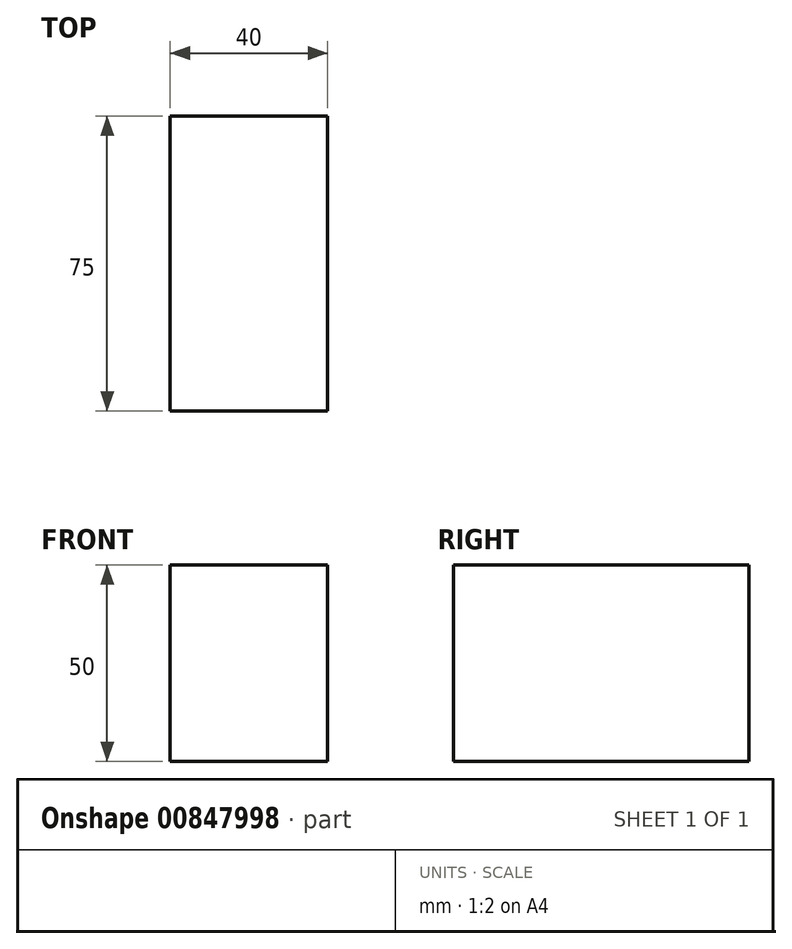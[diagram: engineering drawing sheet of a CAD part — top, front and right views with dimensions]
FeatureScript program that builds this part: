
annotation { "Feature Type Name" : "Feature", "Feature Type Description" : "" }
export const myFeature = defineFeature(function(context is Context, id is Id, definition is map)
    precondition{}
    {
        {
            var Q0;
            Q0=qCreatedBy(makeId("Top.planeOp"),FACE);
            var sketch = newSketch(context, id + "F0", { "sketchPlane" : qUnion([Q0])});
            skLineSegment(sketch, "E0", {"start": v(0, 0) * mm, "end": v(0, 40.88) * mm});
            skLineSegment(sketch, "E1", {"start": v(0, 40.88) * mm, "end": v(40, 40.88) * mm});
            skLineSegment(sketch, "E2", {"start": v(40, 40.88) * mm, "end": v(40, -34.12) * mm});
            skLineSegment(sketch, "E3", {"start": v(40, -34.12) * mm, "end": v(0, -34.12) * mm});
            skLineSegment(sketch, "E4", {"start": v(0, -34.12) * mm, "end": v(0, 0) * mm});
            skSolve(sketch);
        }
        {
            var Q0;
            Q0=makeQuery(id+"F0.imprint","IMPRINT",FACE,{"disambiguationData":[TD([[makeQuery(id+"F0.imprint","IMPRINT",EDGE,{"derivedFrom":sQuery(id+"F0.wireOp",EDGE,"E0")}),-1.0]])]});
            extrude(context, id + "F1", {"entities" : qUnion([Q0]), "depth" : 50 * mm, "offsetDistance" : 25 * mm});
        }
    });
